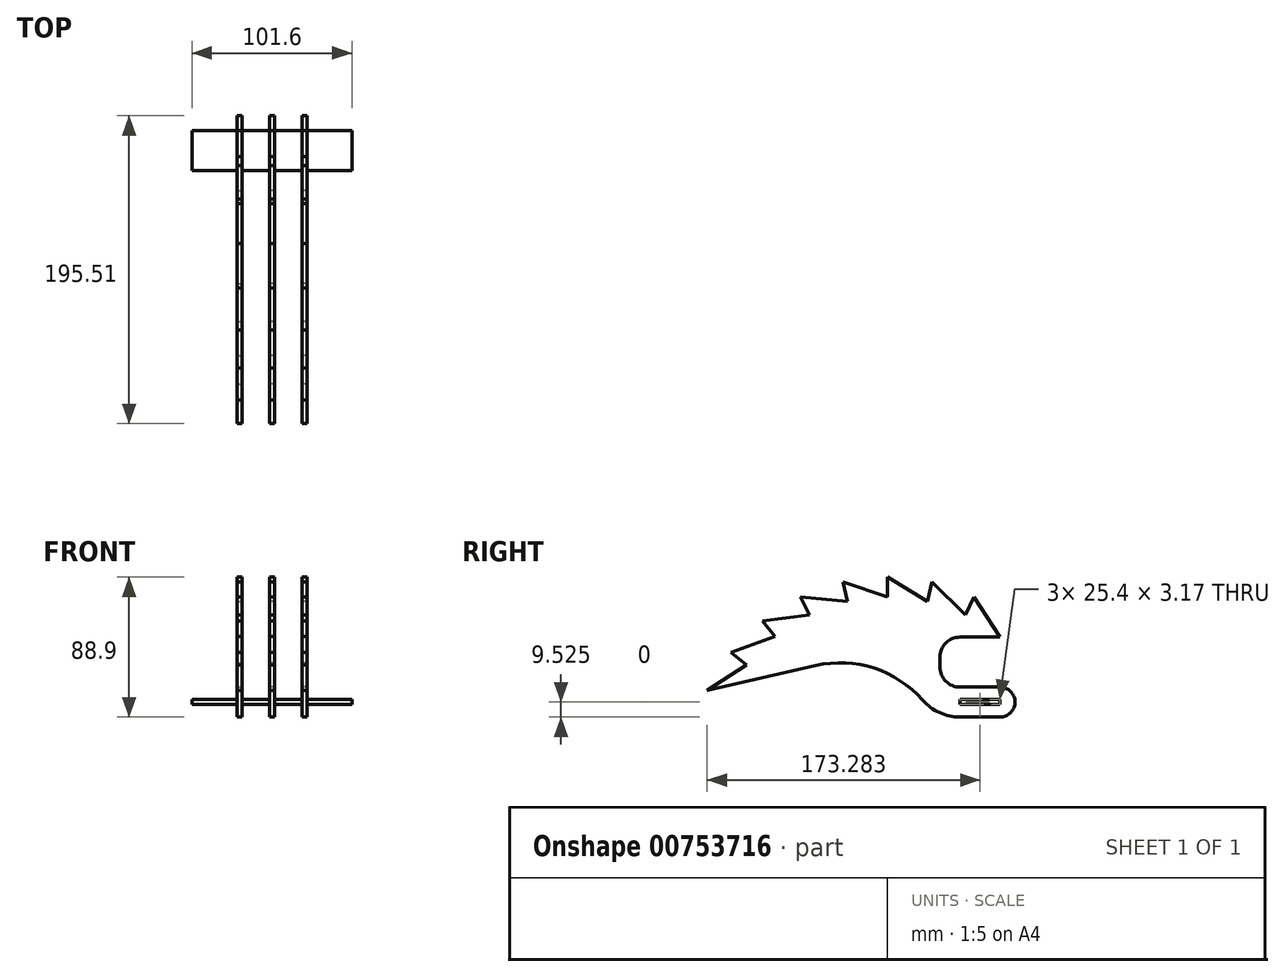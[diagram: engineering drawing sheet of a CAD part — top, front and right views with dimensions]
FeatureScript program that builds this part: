
annotation { "Feature Type Name" : "Feature", "Feature Type Description" : "" }
export const myFeature = defineFeature(function(context is Context, id is Id, definition is map)
    precondition{}
    {
        {
            var Q0;
            Q0=qCreatedBy(makeId("Right.planeOp"),FACE);
            var sketch = newSketch(context, id + "F0", { "sketchPlane" : qUnion([Q0])});
            skCircle(sketch, "E0", {"center": v(0, 0) * mm, "radius": 127 * mm});
            skLineSegment(sketch, "E1", {"start": v(0, 0) * mm, "end": v(-127, 0) * mm, "construction": true});
            skLineSegment(sketch, "E2", {"start": v(-111.43, 25.43) * mm, "end": v(-123.82, 28.26) * mm, "construction": true});
            skLineSegment(sketch, "E3", {"start": v(-102.98, 49.6) * mm, "end": v(-114.42, 55.1) * mm});
            skLineSegment(sketch, "E4", {"start": v(-89.36, 71.26) * mm, "end": v(-99.3, 79.18) * mm});
            skLineSegment(sketch, "E5", {"start": v(-71.27, 89.36) * mm, "end": v(-79.18, 99.3) * mm});
            skLineSegment(sketch, "E6", {"start": v(-49.6, 102.98) * mm, "end": v(-55.1, 114.42) * mm});
            skLineSegment(sketch, "E7", {"start": v(-25.44, 111.43) * mm, "end": v(-28.26, 123.82) * mm});
            skLineSegment(sketch, "E8", {"start": v(71.26, 89.37) * mm, "end": v(79.18, 99.3) * mm});
            skLineSegment(sketch, "E9", {"start": v(89.36, 71.27) * mm, "end": v(99.3, 79.19) * mm});
            skLineSegment(sketch, "E10", {"start": v(102.98, 49.6) * mm, "end": v(114.42, 55.1) * mm});
            skLineSegment(sketch, "E11", {"start": v(0, 0) * mm, "end": v(123.81, 28.26) * mm, "construction": true});
            skLineSegment(sketch, "E12", {"start": v(0, 0) * mm, "end": v(127, 0) * mm, "construction": true});
            skLineSegment(sketch, "E13", {"start": v(-127, 0) * mm, "end": v(-111.43, 25.43) * mm});
            skLineSegment(sketch, "E14", {"start": v(-111.43, 25.43) * mm, "end": v(-123.82, 28.26) * mm});
            skLineSegment(sketch, "E15", {"start": v(-123.82, 28.26) * mm, "end": v(-102.98, 49.6) * mm});
            skLineSegment(sketch, "E16", {"start": v(-102.98, 49.6) * mm, "end": v(-102.98, 49.6) * mm});
            skLineSegment(sketch, "E17", {"start": v(-114.42, 55.1) * mm, "end": v(-89.36, 71.26) * mm});
            skLineSegment(sketch, "E18", {"start": v(-99.3, 79.18) * mm, "end": v(-71.27, 89.36) * mm});
            skLineSegment(sketch, "E19", {"start": v(-79.18, 99.3) * mm, "end": v(-49.6, 102.98) * mm});
            skLineSegment(sketch, "E20", {"start": v(-55.1, 114.42) * mm, "end": v(-25.44, 111.43) * mm});
            skLineSegment(sketch, "E21", {"start": v(-28.26, 123.82) * mm, "end": v(0, 114.3) * mm});
            skLineSegment(sketch, "E22", {"start": v(0, 127) * mm, "end": v(25.43, 111.43) * mm});
            skLineSegment(sketch, "E23", {"start": v(28.26, 123.82) * mm, "end": v(49.6, 102.98) * mm});
            skLineSegment(sketch, "E24", {"start": v(55.1, 114.42) * mm, "end": v(71.26, 89.37) * mm});
            skLineSegment(sketch, "E25", {"start": v(79.18, 99.3) * mm, "end": v(89.36, 71.27) * mm});
            skLineSegment(sketch, "E26", {"start": v(99.3, 79.19) * mm, "end": v(102.98, 49.6) * mm});
            skLineSegment(sketch, "E27.trimOffspring", {"start": v(0, 114.3) * mm, "end": v(0, 127) * mm});
            skLineSegment(sketch, "E28.trimOffspring", {"start": v(25.43, 111.43) * mm, "end": v(28.26, 123.82) * mm});
            skLineSegment(sketch, "E29.trimOffspring", {"start": v(49.6, 102.98) * mm, "end": v(55.1, 114.42) * mm});
            skPoint(sketch, "E30", {"position": v(176.46, 258.8) * mm});
            skPoint(sketch, "E31", {"position": v(165.97, 275.62) * mm});
            skPoint(sketch, "E32.trimOffspring.end.orphan", {"position": v(416.01, 352.08) * mm});
            skPoint(sketch, "E33.center.orphan", {"position": v(265.48, 325) * mm});
            skPoint(sketch, "E34", {"position": v(46.16, 88.9) * mm});
            skLineSegment(sketch, "E35", {"start": v(71.26, 89.37) * mm, "end": v(71.56, 88.9) * mm});
            skArc(sketch, "E36", {"start": v(46.16, 88.9) * mm, "mid": v(37.18, 85.18) * mm, "end": v(33.46, 76.2) * mm});
            skArc(sketch, "E37", {"start": v(33.46, 69.85) * mm, "mid": v(37.18, 60.87) * mm, "end": v(46.16, 57.15) * mm});
            skLineSegment(sketch, "E38", {"start": v(33.46, 76.2) * mm, "end": v(33.46, 69.85) * mm});
            skPoint(sketch, "E39", {"position": v(71.56, 57.15) * mm});
            skLineSegment(sketch, "E40.trimOffspring", {"start": v(46.16, 88.9) * mm, "end": v(71.56, 88.9) * mm});
            skLineSegment(sketch, "E41.trimOffspring", {"start": v(46.16, 57.15) * mm, "end": v(71.56, 57.15) * mm});
            skArc(sketch, "E42", {"start": v(71.56, 57.15) * mm, "mid": v(81.09, 47.62) * mm, "end": v(71.56, 38.1) * mm});
            skArc(sketch, "E43", {"start": v(46.16, 38.1) * mm, "mid": v(33.07, 40.92) * mm, "end": v(22.31, 48.9) * mm});
            skLineSegment(sketch, "E44", {"start": v(71.56, 38.1) * mm, "end": v(46.16, 38.1) * mm});
            skLineSegment(sketch, "E45", {"start": v(-114.42, 55.1) * mm, "end": v(-45.4, 70.8) * mm});
            skArc(sketch, "E46", {"start": v(22.31, 48.9) * mm, "mid": v(-8.53, 69.16) * mm, "end": v(-45.4, 70.8) * mm});
            skSolve(sketch);
        }
        {
            var Q0;
            {var subQ0=sQuery(id+"F0.wireOp",EDGE,"E4");Q0=makeQuery(id+"F0.imprint","IMPRINT",FACE,{"disambiguationData":[TD([[makeQuery(id+"F0.imprint","IMPRINT",EDGE,{"derivedFrom":subQ0}),-1.0]])]});}
            extrude(context, id + "F1", {"entities" : qUnion([Q0]), "depth" : 1.59 * mm, "offsetDistance" : 25.4 * mm, "hasSecondDirection" : true, "secondDirectionOppositeDirection" : true, "secondDirectionDepth" : 1.59 * mm});
        }
        {
            var Q0;
            Q0=makeQuery(id+"F1.opExtrude","CAP_FACE",FACE,{"disambiguationData":[OSD([sQuery(id+"F0.wireOp",EDGE,"E4"),sQuery(id+"F0.wireOp",EDGE,"E5"),sQuery(id+"F0.wireOp",EDGE,"E6"),sQuery(id+"F0.wireOp",EDGE,"E7"),sQuery(id+"F0.wireOp",EDGE,"E17"),sQuery(id+"F0.wireOp",EDGE,"E18"),sQuery(id+"F0.wireOp",EDGE,"E19"),sQuery(id+"F0.wireOp",EDGE,"E20"),sQuery(id+"F0.wireOp",EDGE,"E21"),sQuery(id+"F0.wireOp",EDGE,"E22"),sQuery(id+"F0.wireOp",EDGE,"E23"),sQuery(id+"F0.wireOp",EDGE,"E24"),sQuery(id+"F0.wireOp",EDGE,"E27.trimOffspring"),sQuery(id+"F0.wireOp",EDGE,"E28.trimOffspring"),sQuery(id+"F0.wireOp",EDGE,"E29.trimOffspring"),sQuery(id+"F0.wireOp",EDGE,"E35"),sQuery(id+"F0.wireOp",EDGE,"E36"),sQuery(id+"F0.wireOp",EDGE,"E37"),sQuery(id+"F0.wireOp",EDGE,"E38"),sQuery(id+"F0.wireOp",EDGE,"E40.trimOffspring"),sQuery(id+"F0.wireOp",EDGE,"E41.trimOffspring"),sQuery(id+"F0.wireOp",EDGE,"E42"),sQuery(id+"F0.wireOp",EDGE,"E43"),sQuery(id+"F0.wireOp",EDGE,"E44"),sQuery(id+"F0.wireOp",EDGE,"E45"),sQuery(id+"F0.wireOp",EDGE,"E46")])],"isStart":false});
            extrude(context, id + "F2", {"entities" : qUnion([Q0]), "operationType" : NewBodyOperationType.ADD, "depth" : 20.64 * mm, "offsetDistance" : 25.4 * mm, "hasSecondDirection" : true, "secondDirectionOppositeDirection" : false, "secondDirectionDepth" : 17.46 * mm});
        }
        {
            var Q0;
            Q0=makeQuery(id+"F1.opExtrude","CAP_FACE",FACE,{"disambiguationData":[OSD([sQuery(id+"F0.wireOp",EDGE,"E4"),sQuery(id+"F0.wireOp",EDGE,"E5"),sQuery(id+"F0.wireOp",EDGE,"E6"),sQuery(id+"F0.wireOp",EDGE,"E7"),sQuery(id+"F0.wireOp",EDGE,"E17"),sQuery(id+"F0.wireOp",EDGE,"E18"),sQuery(id+"F0.wireOp",EDGE,"E19"),sQuery(id+"F0.wireOp",EDGE,"E20"),sQuery(id+"F0.wireOp",EDGE,"E21"),sQuery(id+"F0.wireOp",EDGE,"E22"),sQuery(id+"F0.wireOp",EDGE,"E23"),sQuery(id+"F0.wireOp",EDGE,"E24"),sQuery(id+"F0.wireOp",EDGE,"E27.trimOffspring"),sQuery(id+"F0.wireOp",EDGE,"E28.trimOffspring"),sQuery(id+"F0.wireOp",EDGE,"E29.trimOffspring"),sQuery(id+"F0.wireOp",EDGE,"E35"),sQuery(id+"F0.wireOp",EDGE,"E36"),sQuery(id+"F0.wireOp",EDGE,"E37"),sQuery(id+"F0.wireOp",EDGE,"E38"),sQuery(id+"F0.wireOp",EDGE,"E40.trimOffspring"),sQuery(id+"F0.wireOp",EDGE,"E41.trimOffspring"),sQuery(id+"F0.wireOp",EDGE,"E42"),sQuery(id+"F0.wireOp",EDGE,"E43"),sQuery(id+"F0.wireOp",EDGE,"E44"),sQuery(id+"F0.wireOp",EDGE,"E45"),sQuery(id+"F0.wireOp",EDGE,"E46")])],"isStart":true});
            extrude(context, id + "F3", {"entities" : qUnion([Q0]), "depth" : 20.64 * mm, "offsetDistance" : 25.4 * mm, "hasSecondDirection" : true, "secondDirectionOppositeDirection" : false, "secondDirectionDepth" : 17.46 * mm});
        }
        {
            var Q0;
            Q0=makeQuery(id+"F0.imprint","IMPRINT",FACE,{"disambiguationData":[TD([[makeQuery(id+"F0.imprint","IMPRINT",EDGE,{"derivedFrom":sQuery(id+"F0.wireOp",EDGE,"E3")}),-1.0]])]});
            var sketch = newSketch(context, id + "F4", { "sketchPlane" : qUnion([Q0])});
            skLineSegment(sketch, "E47.bottom", {"start": v(71.56, 46.04) * mm, "end": v(46.16, 46.04) * mm});
            skLineSegment(sketch, "E47.top", {"start": v(71.56, 49.21) * mm, "end": v(46.16, 49.21) * mm});
            skLineSegment(sketch, "E47.left", {"start": v(71.56, 46.04) * mm, "end": v(71.56, 49.21) * mm});
            skLineSegment(sketch, "E47.right", {"start": v(46.16, 46.04) * mm, "end": v(46.16, 49.21) * mm});
            skPoint(sketch, "E47.middle", {"position": v(58.86, 47.62) * mm});
            skSolve(sketch);
        }
        {
            var Q0;
            Q0 = qSketchRegion(id + "F4", true);
            extrude(context, id + "F5", {"entities" : qUnion([Q0]), "operationType" : NewBodyOperationType.ADD, "depth" : 50.8 * mm, "offsetDistance" : 25.4 * mm, "hasSecondDirection" : true, "secondDirectionOppositeDirection" : true, "secondDirectionDepth" : 50.8 * mm});
        }
    });
